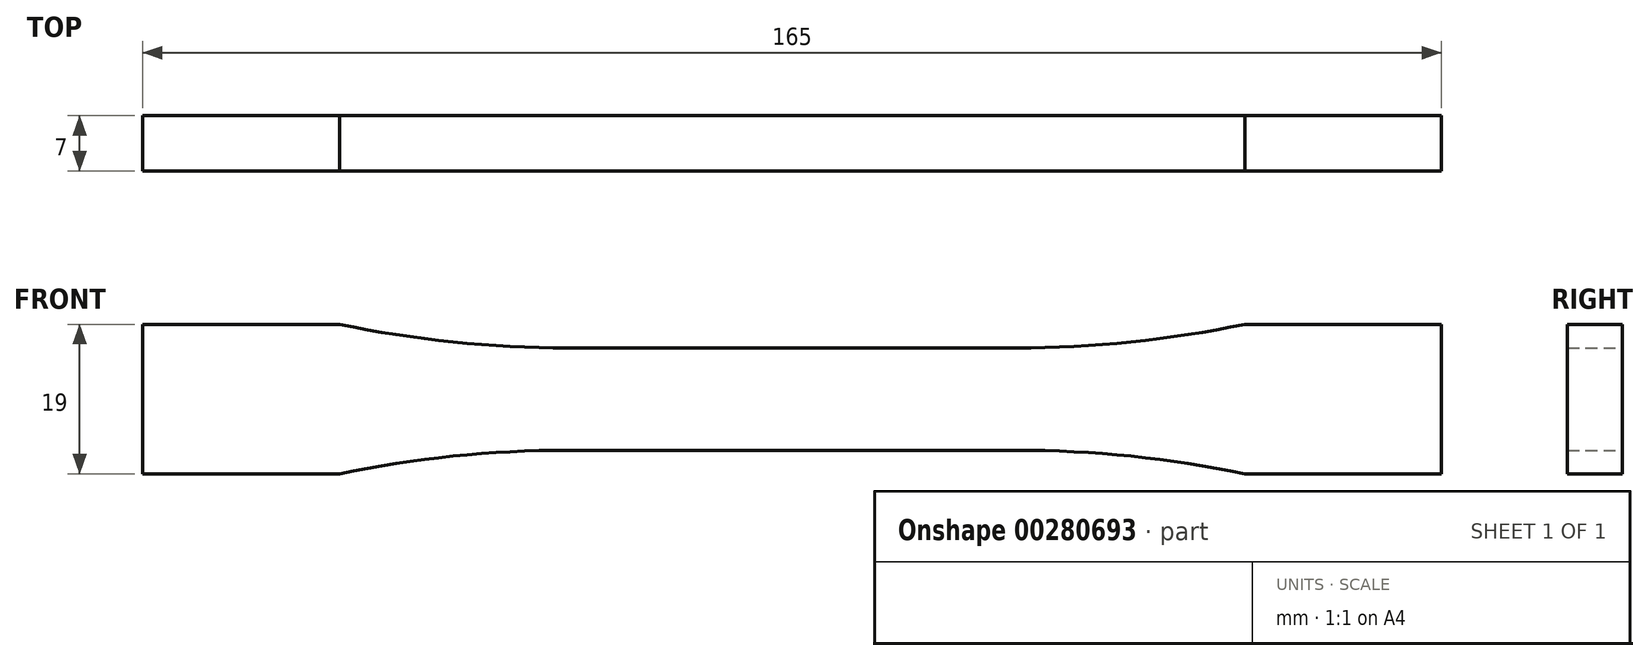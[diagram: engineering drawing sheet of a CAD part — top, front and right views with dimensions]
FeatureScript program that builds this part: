
annotation { "Feature Type Name" : "Feature", "Feature Type Description" : "" }
export const myFeature = defineFeature(function(context is Context, id is Id, definition is map)
    precondition{}
    {
        {
            var Q0;
            Q0=qCreatedBy(makeId("Front.planeOp"),FACE);
            var sketch = newSketch(context, id + "F0", { "sketchPlane" : qUnion([Q0])});
            skLineSegment(sketch, "E0", {"start": v(0, 6.5) * mm, "end": v(28.5, 6.5) * mm});
            skLineSegment(sketch, "E1", {"start": v(57.5, 9.5) * mm, "end": v(82.5, 9.5) * mm});
            skLineSegment(sketch, "E2", {"start": v(82.5, 9.5) * mm, "end": v(82.5, 0) * mm});
            skArc(sketch, "E3", {"start": v(28.5, 6.5) * mm, "mid": v(43.08, 7.25) * mm, "end": v(57.5, 9.5) * mm});
            skLineSegment(sketch, "E4.MirrorCS", {"start": v(57.5, -9.5) * mm, "end": v(82.5, -9.5) * mm});
            skArc(sketch, "E5.MirrorCS", {"start": v(28.5, -6.5) * mm, "mid": v(43.08, -7.25) * mm, "end": v(57.5, -9.5) * mm});
            skLineSegment(sketch, "E6.MirrorCS", {"start": v(82.5, -9.5) * mm, "end": v(82.5, 0) * mm});
            skLineSegment(sketch, "E7.MirrorCS", {"start": v(0, -6.5) * mm, "end": v(28.5, -6.5) * mm});
            skLineSegment(sketch, "E8.MirrorCS", {"start": v(0, -6.5) * mm, "end": v(-28.5, -6.5) * mm});
            skLineSegment(sketch, "E9.MirrorCS", {"start": v(-82.5, -9.5) * mm, "end": v(-82.5, 0) * mm});
            skLineSegment(sketch, "E10.MirrorCS", {"start": v(0, 6.5) * mm, "end": v(-28.5, 6.5) * mm});
            skLineSegment(sketch, "E11.MirrorCS", {"start": v(-57.5, 9.5) * mm, "end": v(-82.5, 9.5) * mm});
            skLineSegment(sketch, "E12.MirrorCS", {"start": v(-82.5, 9.5) * mm, "end": v(-82.5, 0) * mm});
            skArc(sketch, "E13.MirrorCS", {"start": v(-28.5, -6.5) * mm, "mid": v(-43.08, -7.25) * mm, "end": v(-57.5, -9.5) * mm});
            skLineSegment(sketch, "E14.MirrorCS", {"start": v(-57.5, -9.5) * mm, "end": v(-82.5, -9.5) * mm});
            skArc(sketch, "E15.MirrorCS", {"start": v(-28.5, 6.5) * mm, "mid": v(-43.08, 7.25) * mm, "end": v(-57.5, 9.5) * mm});
            skSolve(sketch);
        }
        {
            var Q0;
            Q0 = qSketchRegion(id + "F0", true);
            extrude(context, id + "F1", {"entities" : qUnion([Q0]), "depth" : 7 * mm});
        }
    });
